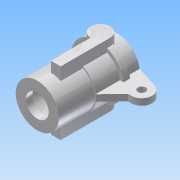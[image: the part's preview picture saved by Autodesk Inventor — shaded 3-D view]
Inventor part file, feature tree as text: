
AUTODESK INVENTOR PART (.ipt)
format: ipt  version: 2014 (Build 180170000, 170)  size: 225,280 bytes
history: native  units: in
note: dims shown in document units (in); Inventor stores cm internally (conversion verified against a paired STEP export)
features: extrude x9, sketch x9, plane x2, mirror x1
ambient origin geometry x8: Origin, YZ Plane, XZ Plane, XY Plane, X Axis, Y Axis, Z Axis, Center Point
bodies: Solid1 (feature_tree)
feature tree (21):
  extrude  "Extrusion1"  Depth=0.55in TaperAngle=0.0deg
  extrude  "Extrusion2"  Depth=0.67in TaperAngle=0.0deg
  plane  "Work Plane1"
  extrude  "Extrusion3"  Depth=0.81in
  extrude  "Extrusion7"  Depth=0.55in
  extrude  "Extrusion8"  Depth=0.35in
  extrude  "Extrusion9"  Depth=0.1in TaperAngle=0.0deg
  extrude  "Extrusion11"  Depth=0.32in
  extrude  "Extrusion12"  Depth=0.64in
  plane  "Work Plane8"
  extrude  "Extrusion13"  Depth=0.15in TaperAngle=0.0deg
  mirror  "Mirror2"
  sketch  "Sketch2"  dims[d0=0.66in d1=0.55in d2=0.0in]
  sketch  "Sketch3"  dims[d3=0.7in d4=0.67in d5=0.0in]
  sketch  "Sketch4"  dims[d6=-0.37in d7=0.81in]
  sketch  "Sketch9"  dims[d8=0.1in d9=0.0in d40=0.55in]
  sketch  "Sketch10"  dims[d41=1.12in d42=0.0in d43=0.35in]
  sketch  "Sketch12"  dims[d44=1.12in d45=0.0in d50=0.1in d51=0.0in]
  sketch  "Sketch14"  dims[d54=0.12in d55=0.32in]
  sketch  "Sketch15"  dims[d56=0.26in d57=0.64in]
  sketch  "Sketch16"  dims[d58=1.0in d59=0.0in d60=1.0in d61=0.0in d62=0.489in d63=0.3in d65=0.15in d66=0.21in d67=1.0in d68=0.0in]
